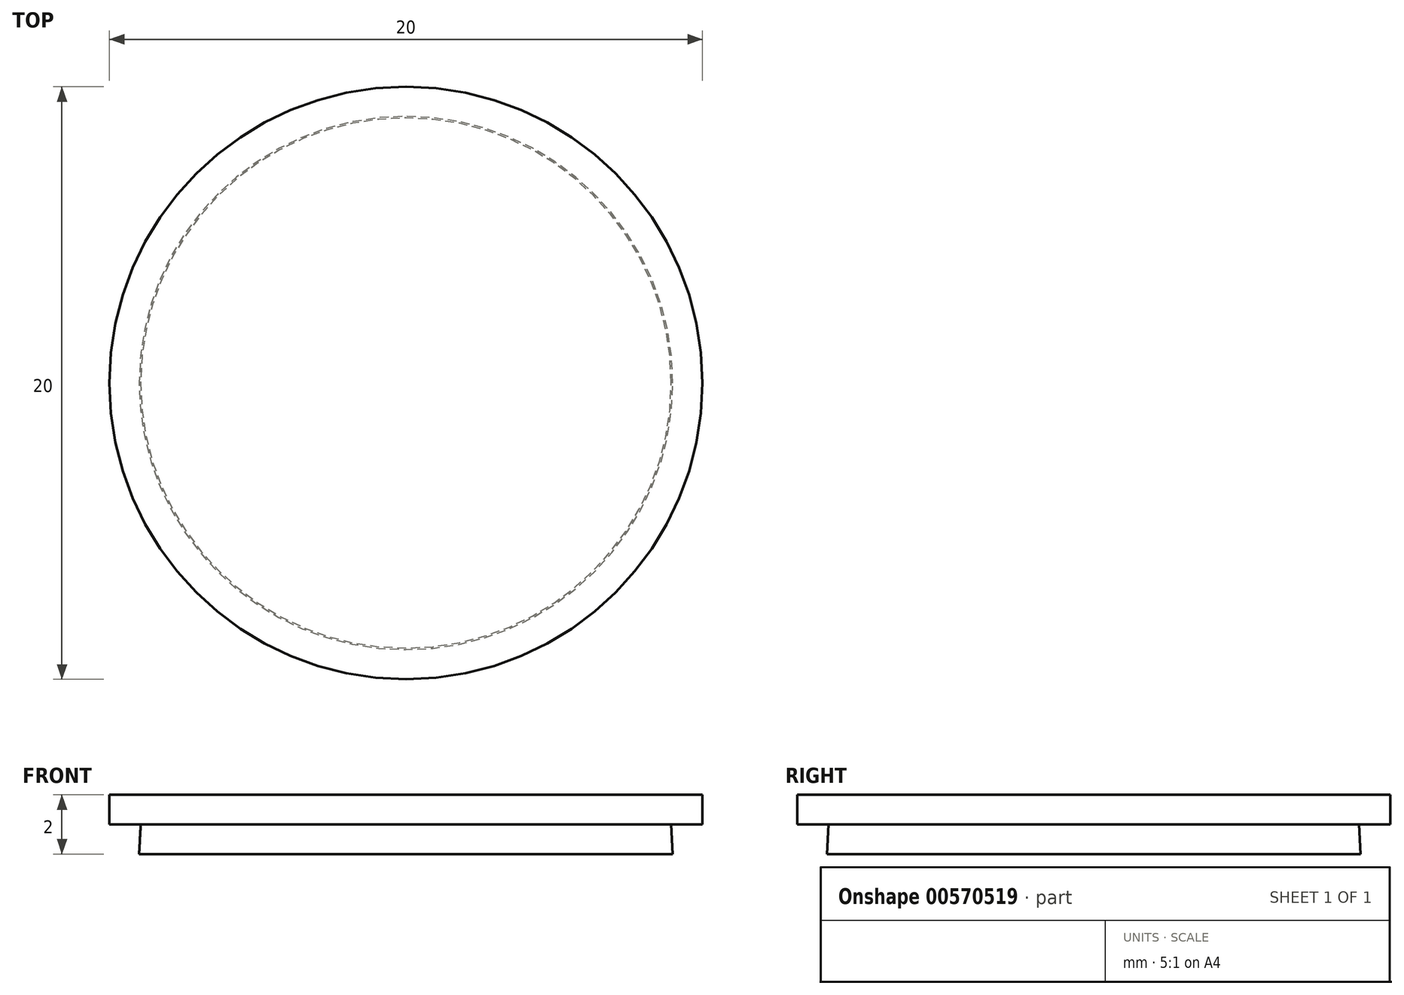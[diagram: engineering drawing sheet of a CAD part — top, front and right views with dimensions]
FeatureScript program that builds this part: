
annotation { "Feature Type Name" : "Feature", "Feature Type Description" : "" }
export const myFeature = defineFeature(function(context is Context, id is Id, definition is map)
    precondition{}
    {
        {
            var Q0;
            Q0=qCreatedBy(makeId("Top.planeOp"),FACE);
            var sketch = newSketch(context, id + "F0", { "sketchPlane" : qUnion([Q0])});
            skCircle(sketch, "E0", {"center": v(0, 0) * mm, "radius": 10 * mm});
            skSolve(sketch);
        }
        {
            var Q0;
            Q0=makeQuery(id+"F0.imprint","IMPRINT",FACE,{"disambiguationData":[TD([[makeQuery(id+"F0.imprint","IMPRINT",EDGE,{"derivedFrom":sQuery(id+"F0.wireOp",EDGE,"E0")}),1.0]])]});
            extrude(context, id + "F1", {"entities" : qUnion([Q0]), "depth" : 2 * mm, "offsetDistance" : 25.4 * mm});
        }
        {
            var Q0;
            Q0=makeQuery(id+"F1.opExtrude","CAP_FACE",FACE,{"disambiguationData":[OSD([sQuery(id+"F0.wireOp",EDGE,"E0")])],"isStart":true});
            var sketch = newSketch(context, id + "F2", { "sketchPlane" : qUnion([Q0])});
            skCircle(sketch, "E1", {"center": v(0, 0) * mm, "radius": 9 * mm});
            skSolve(sketch);
        }
        {
            var Q0;
            Q0=makeQuery(id+"F2.imprint","IMPRINT",FACE,{"disambiguationData":[TD([[makeQuery(id+"F2.imprint","IMPRINT",EDGE,{"derivedFrom":sQuery(id+"F2.wireOp",EDGE,"E1")}),-1.0]])]});
            extrude(context, id + "F3", {"entities" : qUnion([Q0]), "operationType" : NewBodyOperationType.REMOVE, "oppositeDirection" : true, "depth" : 1 * mm, "offsetDistance" : 25 * mm, "hasDraft" : true, "draftAngle" : 3 * degree});
        }
    });
